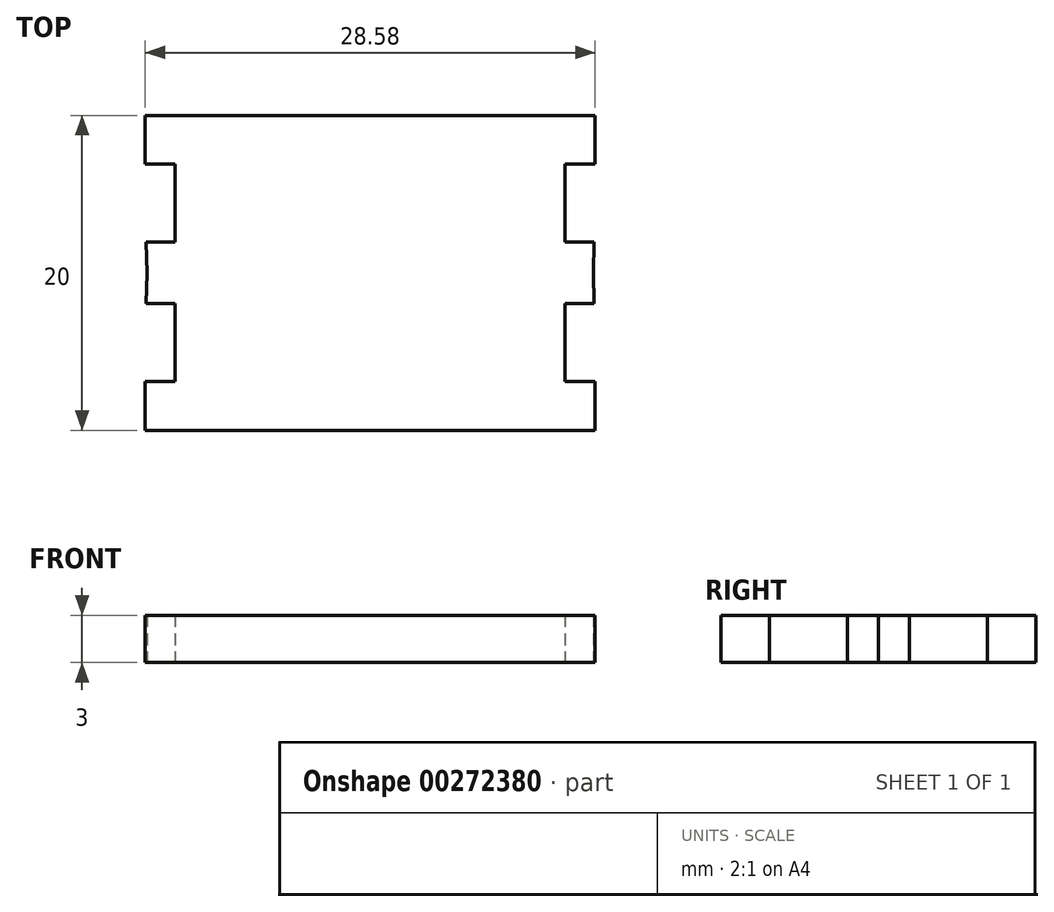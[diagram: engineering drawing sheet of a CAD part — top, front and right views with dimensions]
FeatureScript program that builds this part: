
annotation { "Feature Type Name" : "Feature", "Feature Type Description" : "" }
export const myFeature = defineFeature(function(context is Context, id is Id, definition is map)
    precondition{}
    {
        {
            var Q0;
            Q0=qCreatedBy(makeId("Top.planeOp"),FACE);
            var sketch = newSketch(context, id + "F0", { "sketchPlane" : qUnion([Q0])});
            skLineSegment(sketch, "E0.bottom", {"start": v(14.29, 10) * mm, "end": v(-14.29, 10) * mm});
            skLineSegment(sketch, "E0.top", {"start": v(14.29, -10) * mm, "end": v(-14.29, -10) * mm});
            skPoint(sketch, "E0.middle", {"position": v(0, 0) * mm});
            skLineSegment(sketch, "E1", {"start": v(0, 10) * mm, "end": v(0, -10) * mm, "construction": true});
            skLineSegment(sketch, "E2", {"start": v(-14.18, 0) * mm, "end": v(14.29, 0) * mm, "construction": true});
            skLineSegment(sketch, "E3", {"start": v(-14.29, 10) * mm, "end": v(-14.29, 6.92) * mm});
            skLineSegment(sketch, "E4", {"start": v(-14.29, 6.92) * mm, "end": v(-12.39, 6.92) * mm});
            skLineSegment(sketch, "E5", {"start": v(-12.39, 6.92) * mm, "end": v(-12.39, 1.96) * mm});
            skLineSegment(sketch, "E6", {"start": v(-12.39, 1.96) * mm, "end": v(-14.23, 1.96) * mm});
            skLineSegment(sketch, "E7", {"start": v(-14.23, 1.96) * mm, "end": v(-14.18, 0) * mm});
            skLineSegment(sketch, "E8.MirrorCS", {"start": v(-14.23, -1.96) * mm, "end": v(-14.18, 0) * mm});
            skLineSegment(sketch, "E9.MirrorCS", {"start": v(-12.39, -1.96) * mm, "end": v(-14.23, -1.96) * mm});
            skLineSegment(sketch, "E10.MirrorCS", {"start": v(-12.39, -6.92) * mm, "end": v(-12.39, -1.96) * mm});
            skLineSegment(sketch, "E11.MirrorCS", {"start": v(-14.29, -10) * mm, "end": v(-14.29, -6.92) * mm});
            skLineSegment(sketch, "E12.MirrorCS", {"start": v(-14.29, -6.92) * mm, "end": v(-12.39, -6.92) * mm});
            skLineSegment(sketch, "E13.MirrorCS", {"start": v(14.29, -10) * mm, "end": v(14.29, -6.92) * mm});
            skLineSegment(sketch, "E14.MirrorCS", {"start": v(14.29, -6.92) * mm, "end": v(12.39, -6.92) * mm});
            skLineSegment(sketch, "E15.MirrorCS", {"start": v(12.39, -6.92) * mm, "end": v(12.39, -1.96) * mm});
            skLineSegment(sketch, "E16.MirrorCS", {"start": v(12.39, -1.96) * mm, "end": v(14.23, -1.96) * mm});
            skLineSegment(sketch, "E17.MirrorCS", {"start": v(14.23, -1.96) * mm, "end": v(14.18, 0) * mm});
            skLineSegment(sketch, "E18.MirrorCS", {"start": v(14.23, 1.96) * mm, "end": v(14.18, 0) * mm});
            skLineSegment(sketch, "E19.MirrorCS", {"start": v(12.39, 1.96) * mm, "end": v(14.23, 1.96) * mm});
            skLineSegment(sketch, "E20.MirrorCS", {"start": v(14.29, 6.92) * mm, "end": v(12.39, 6.92) * mm});
            skLineSegment(sketch, "E21.MirrorCS", {"start": v(14.29, 10) * mm, "end": v(14.29, 6.92) * mm});
            skLineSegment(sketch, "E22.MirrorCS", {"start": v(12.39, 6.92) * mm, "end": v(12.39, 1.96) * mm});
            skSolve(sketch);
        }
        {
            var Q0;
            Q0=makeQuery(id+"F0.imprint","IMPRINT",FACE,{"disambiguationData":[TD([[makeQuery(id+"F0.imprint","IMPRINT",EDGE,{"derivedFrom":sQuery(id+"F0.wireOp",EDGE,"E0.bottom")}),1.0]])]});
            extrude(context, id + "F1", {"entities" : qUnion([Q0]), "depth" : 3 * mm});
        }
    });
